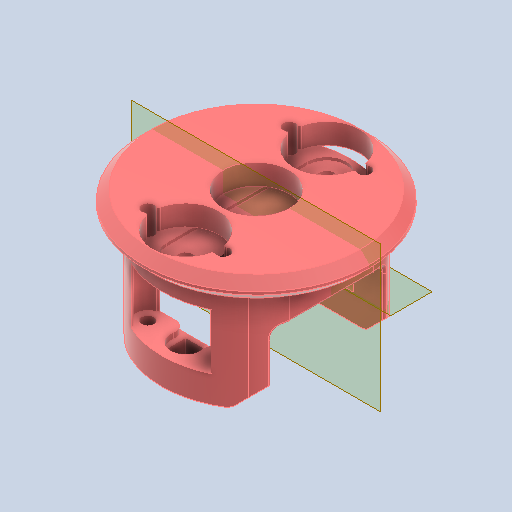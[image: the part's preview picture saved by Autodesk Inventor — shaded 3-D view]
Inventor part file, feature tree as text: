
AUTODESK INVENTOR PART (.ipt)
format: ipt  version: 2022 (Build 260153000, 153)  size: 1,040,896 bytes
history: native  units: in
note: dims shown in document units (in); Inventor stores cm internally (conversion verified against a paired STEP export)
features: extrude x14, sketch x13, fillet x5, projected_geometry x5, mirror x4, other x4, plane x3, reference x2, chamfer x1
ambient origin geometry x8: Origin, YZ Plane, XZ Plane, XY Plane, X Axis, Y Axis, Z Axis, Center Point
bodies: Solid1 (feature_tree)
feature tree (51):
  extrude  "Extrusion1"  Depth=0.2756in TaperAngle=0.0deg
  extrude  "Extrusion2"  Depth=4.0in
  extrude  "Extrusion10"  Depth=1.3681in TaperAngle=0.0deg
  sketch  "Sketch6"  dims[d5=0.25in d6=1.3681in d7=0.0in]
  extrude  "Extrusion6"  Depth=1.0in
  extrude  "Extrusion7"  Depth=0.7874in TaperAngle=360.0deg
  plane  "Work Plane6"
  plane  "Work Plane7"
  extrude  "Extrusion8"  Depth=0.05in TaperAngle=0.0deg
  extrude  "Extrusion9"  [1 undecoded]
  extrude  "Extrusion11"  Depth=1.125in
  fillet  "Fillet3"  Radius=0.3238in
  fillet  "Fillet4"  Radius=0.1in
  fillet  "Fillet5"  Radius=3.0in
  plane  "Work Plane8"
  mirror  "Mirror2"
  extrude  "Extrusion12"  TaperAngle=45.0deg  [1 undecoded]
  mirror  "Mirror3"
  extrude  "Extrusion13"  TaperAngle=0.0deg  [1 undecoded]
  fillet  "Fillet6"  Radius=0.5in
  extrude  "Extrusion14"  Depth=0.125in
  chamfer  "Chamfer2"  Distance=0.5in
  extrude  "Extrusion15"  Depth=0.125in
  mirror  "Mirror4"
  extrude  "Extrusion16"  Depth=0.125in TaperAngle=0.0deg
  extrude  "Extrusion17"  Depth=0.125in
  fillet  "Fillet8"  Radius=0.0472in
  mirror  "Mirror5"
  sketch  "Sketch1"  dims[d0=2.9941in d1=0.2756in d2=0.0in]
  sketch  "Sketch2"  dims[d3=1.5in d4=4.0in]
  projected_geometry  "Projected Loop1"
  sketch  "Sketch7"  dims[d40=0.1839in d41=1.0in]
  sketch  "Sketch8"  dims[d42=0.1679in d43=0.7874in d45=360.0deg]
  reference  "Reference1"
  sketch  "Sketch9"  dims[d47=1.5in d48=0.0in d49=0.05in d50=0.0in]
  projected_geometry  "Projected Loop8"
  sketch  "Sketch10"  dims[d51=0.1749in d52=-0.3556in]
  sketch  "Sketch11"  dims[d55=0.7356in d56=0.0in d57=1.125in d58=0.3238in d59=0.1in d60=0.0in d61=3.0in]
  reference  "Reference2"
  sketch  "Sketch12"  dims[d62=1.0in d63=0.0in d64=45.0deg]
  sketch  "Sketch13"  dims[d65=45.0deg d66=0.0in d67=0.0in d68=0.5in]
  sketch  "Sketch14"  dims[d69=0.125in d70=0.0236in]
  projected_geometry  "Projected Loop9"
  sketch  "Sketch15"  dims[d71=0.1852in]
  projected_geometry  "Projected Loop10"
  sketch  "Sketch16"  dims[d72=0.2in d73=0.5in d74=0.0in d75=0.876in d76=0.2756in d77=0.0in d78=0.0236in d80=0.0472in d81=0.0in d82=0.2559in d84=0.1181in d85=0.125in d86=45.0deg d87=0.1014in d88=0.0in d89=0.3957in d90=0.261in d91=0.0787in d92=0.0in d93=0.261in d94=0.3937in d95=0.0in d96=0.125in d22=0.5in d23=0.0344in d24=0.5in d25=0.0344in d79=0.0344in]
  projected_geometry  "Projected Loop11"
  other  "<userpath>\Documents\CAD\guardSwerve1\Assembly1.iam"
  other  "Assembly1.iam"
  other  "SScrew Star Smooth .750:2"
  other  "2.75 Traction, No Insert:1"
note: 3 required parameter values undecoded (feature->parameter linkage not recoverable at this tier; creation-order binding heuristic only, values carry confidence <= 0.55)
